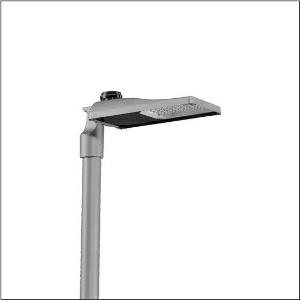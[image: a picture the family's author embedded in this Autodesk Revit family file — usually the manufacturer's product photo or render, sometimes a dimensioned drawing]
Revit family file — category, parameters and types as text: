
# Revit family: streetlight_sl_31_mini___st1_0a_5xh2d3bn08ja_dd0a
name_source: partatom
category: Lighting Fixtures
units: mm (PartAtom-declared; Revit-internal decimal feet)

## family parameters
Cut with Voids When Loaded = No
Host = Face
Light Source = No
Part Type = Normal
Room Calculation Point = No
Round Connector Dimension = Use Diameter
Shared = No

## types (1)
- --- (1 x LED, 12140 lm, 81.1 W, 3000K)
    Apparent Load = 81 VA
    CIE Flux Codes = 40 73 97 100 100
    Color Rendering = 70
    Color Temperature = 3000K
    Default Elevation = 1800 mm
    Description = Streetlight SL 31 mini NEMA (7pin) mast luminaire for post-top, side-entry; light control with lens of PMMA; light distribution: ST1.0a, direct asymmetric distribution, for standard-compliant lighting for roads and squares; LED: luminous flux: 12.140lm, light colour: 730, colour temperature: 3000K; luminous efficacy: 149,7lm/W; control: overheat protection, intelligent temperature release in ECG and LED module, constant luminous flux control, time-dependent luminous flux control, flexible luminous flux parameterisation, pre-setting: linear dimming characteristic; luminaire housing, of diecast aluminium, Siteco® metallic grey (DB 702S), corrosivity category C5 high according to DIN EN ISO 12944; cover of toughened safety glass, transparent, mast flange of diecast aluminium, Siteco® metallic grey (DB 702S), spigot size: 76/60mm, mast flange included unmounted; with cable H07RN-F 3x 1.5mm², cable length: 10,5m, connection cable pre-assembled; mains connection: 220..240V, AC, 50/60Hz; power consumption (at start of service life): 81,1W / (at end of service life): 88,3W / (with reduced operation 50%): 36,4W; protection rating (complete): IP66; insulation class (complete): insulation class I (protective earthing); impact resistance: IK10; certification: CE, ENEC, ENEC+, VDE, UKCA; permissible operating ambient temperature for outdoor applications: -40..+50°C; packaging unit: 1 piece

Light Distribution: ST1.0a
    Height = 76 mm
    Lamp = 1 x LED
    Lamp Light Flux = 12140 lm
    Lamp Power = 81.1 W
    Lamp count = 1
    Length = 547 mm
    Luminous efficacy = 150 lm/W
    Manufacturer = Siteco
    ModVariant = No
    Model = 5XH2D3BN08JA
    Number of Poles = 1
    OnlyDefault = Yes
    Power Factor = 1
    Product Name = Streetlight SL 31 mini | ST1.0a
    Product group = mast luminaire | pylon top
    ProductGroupID = 6100
    Protection Class = Protection class I
    Protection Degree = IP 66
    RLX_Detail_Level = 1
    RLX_Emergency_Light_Flux = 0 lm
    RLX_Emergency_Type = 0
    RLX_Emergency_Type_DB = No
    RlxData = <blob elided: 40241 chars, md5=5df475ed>
    Socket = socket
    Standby Power = 0 W
    System Light Flux = 12140 lm
    System Power = 81 W
    Type Comments = factory setting: luminous flux: 100 % | dim-lin: 254 | 860 mA
    Type Image = l_1300322.jpg
    URL = http://relux.com
    VarID = @adj_050646
    Voltage = 0 V
    Weight = 0.00 kg
    Width = 265 mm

## geometry (parser evidence)
native form markers: Blend x4, Sweep x10
no freeform markers — native parametric forms only
